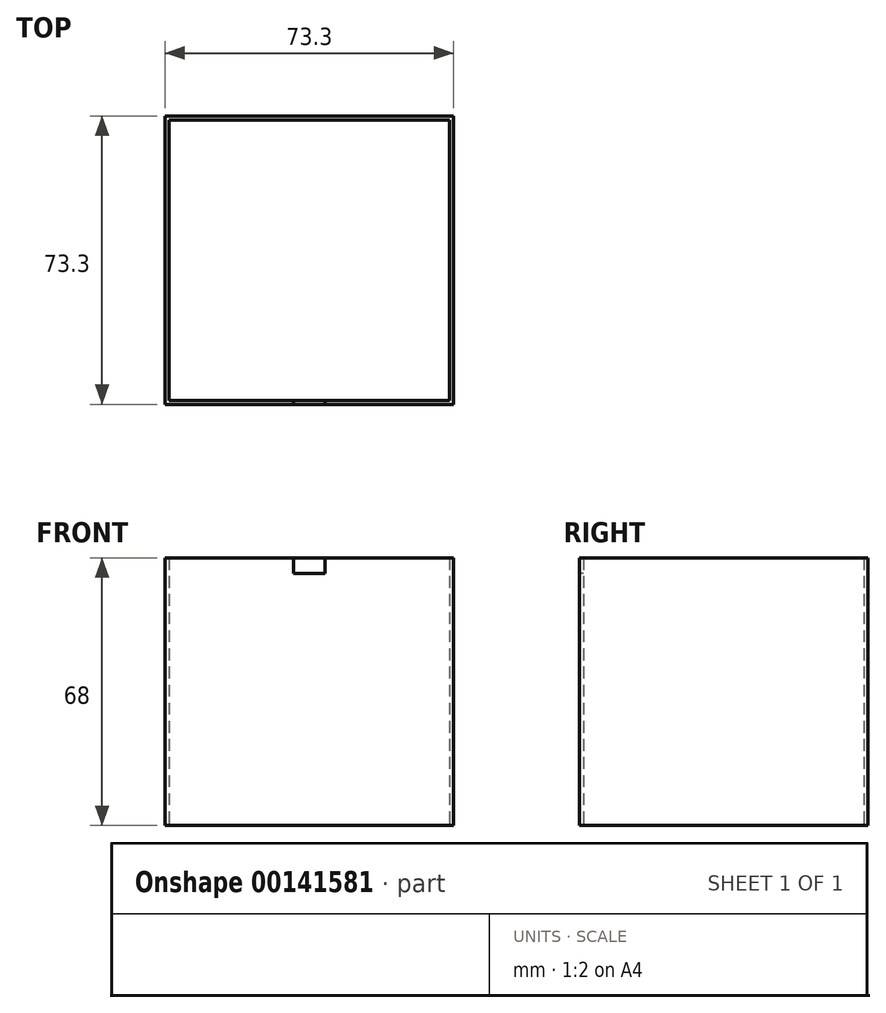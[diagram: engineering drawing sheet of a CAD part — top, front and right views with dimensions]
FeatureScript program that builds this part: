
annotation { "Feature Type Name" : "Feature", "Feature Type Description" : "" }
export const myFeature = defineFeature(function(context is Context, id is Id, definition is map)
    precondition{}
    {
        {
            var Q0;
            Q0=qCreatedBy(makeId("Top.planeOp"),FACE);
            var sketch = newSketch(context, id + "F0", { "sketchPlane" : qUnion([Q0])});
            skLineSegment(sketch, "E0.bottom", {"start": v(0, 0) * mm, "end": v(73.3, 0) * mm});
            skLineSegment(sketch, "E0.top", {"start": v(0, -73.3) * mm, "end": v(73.3, -73.3) * mm});
            skLineSegment(sketch, "E0.left", {"start": v(0, 0) * mm, "end": v(0, -73.3) * mm});
            skLineSegment(sketch, "E0.right", {"start": v(73.3, 0) * mm, "end": v(73.3, -73.3) * mm});
            skLineSegment(sketch, "E1.bottom", {"start": v(1, -1) * mm, "end": v(72.3, -1) * mm});
            skLineSegment(sketch, "E1.top", {"start": v(1, -72.3) * mm, "end": v(72.3, -72.3) * mm});
            skLineSegment(sketch, "E1.left", {"start": v(1, -1) * mm, "end": v(1, -72.3) * mm});
            skLineSegment(sketch, "E1.right", {"start": v(72.3, -1) * mm, "end": v(72.3, -72.3) * mm});
            skLineSegment(sketch, "E2", {"start": v(1, -1) * mm, "end": v(1, 0) * mm, "construction": true});
            skLineSegment(sketch, "E3", {"start": v(1, -1) * mm, "end": v(0, -1) * mm, "construction": true});
            skLineSegment(sketch, "E4", {"start": v(72.3, -72.3) * mm, "end": v(72.3, -73.3) * mm, "construction": true});
            skLineSegment(sketch, "E5", {"start": v(72.3, -72.3) * mm, "end": v(73.3, -72.3) * mm, "construction": true});
            skSolve(sketch);
        }
        {
            var Q0;
            Q0=makeQuery(id+"F0.imprint","IMPRINT",FACE,{"disambiguationData":[TD([[makeQuery(id+"F0.imprint","IMPRINT",EDGE,{"derivedFrom":sQuery(id+"F0.wireOp",EDGE,"E0.bottom")}),-1.0]])]});
            var Q1;
            Q1=sQuery(id+"F0.wireOp",EDGE,"E1.left");
            extrude(context, id + "F1", {"entities" : qUnion([Q0]), "surfaceEntities" : qUnion([Q1]), "depth" : 68 * mm});
        }
        {
            var Q0;
            Q0=makeQuery(id+"F1.opExtrude","SWEPT_FACE",FACE,{"disambiguationData":[OSD([sQuery(id+"F0.wireOp",EDGE,"E0.top")])]});
            var sketch = newSketch(context, id + "F2", { "sketchPlane" : qUnion([Q0])});
            skPoint(sketch, "E6.endSnap0", {"position": v(36.65, 68) * mm});
            skLineSegment(sketch, "E7", {"start": v(36.65, 64) * mm, "end": v(32.65, 64) * mm});
            skLineSegment(sketch, "E8", {"start": v(32.65, 64) * mm, "end": v(32.65, 68) * mm});
            skLineSegment(sketch, "E9", {"start": v(36.65, 64) * mm, "end": v(40.65, 64) * mm});
            skLineSegment(sketch, "E10", {"start": v(40.65, 64) * mm, "end": v(40.65, 68) * mm});
            skSolve(sketch);
        }
        {
            var Q0;
            Q0=qSketchRegion(id+"F2",true);
            var Q1;
            Q1=makeQuery(id+"F2.imprint","IMPRINT",FACE,{"disambiguationData":[TD([[makeQuery(id+"F2.imprint","IMPRINT",EDGE,{"derivedFrom":sQuery(id+"F2.wireOp",EDGE,"E7")}),-1.0]])]});
            extrude(context, id + "F3", {"entities" : qUnion([Q0, Q1]), "operationType" : NewBodyOperationType.REMOVE, "oppositeDirection" : true, "depth" : 5 * mm});
        }
    });
